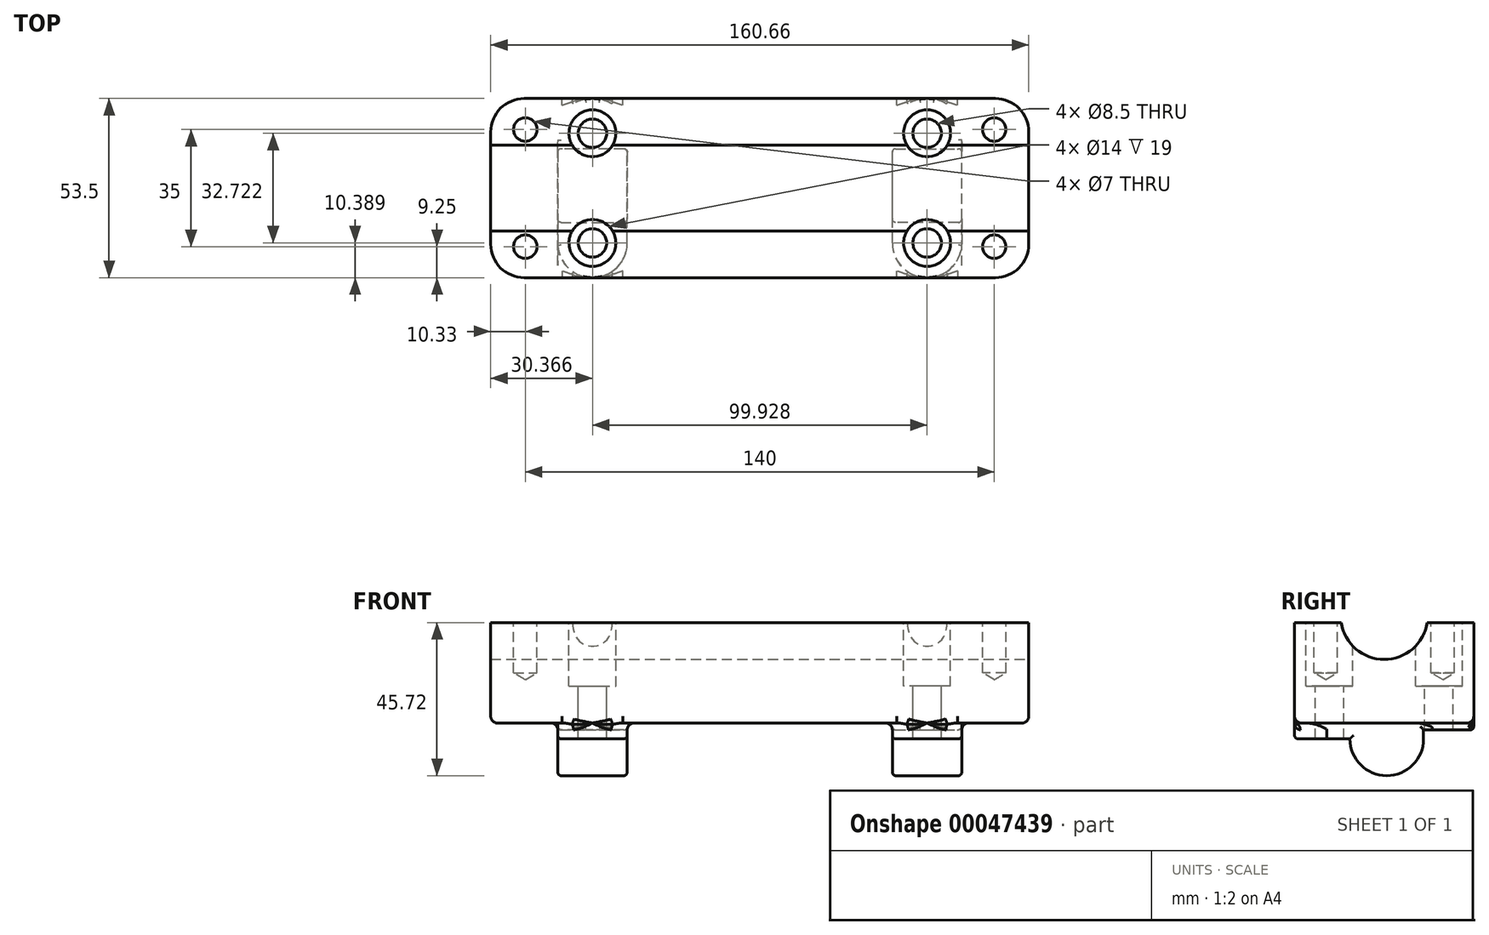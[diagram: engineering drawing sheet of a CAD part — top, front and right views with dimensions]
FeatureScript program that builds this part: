
annotation { "Feature Type Name" : "Feature", "Feature Type Description" : "" }
export const myFeature = defineFeature(function(context is Context, id is Id, definition is map)
    precondition{}
    {
        {
            var Q0;
            Q0=qCreatedBy(makeId("Right.planeOp"),FACE);
            var sketch = newSketch(context, id + "F0", { "sketchPlane" : qUnion([Q0])});
            skLineSegment(sketch, "E0.rect.bottom", {"start": v(-26.75, 15) * mm, "end": v(26.75, 15) * mm});
            skLineSegment(sketch, "E0.rect.top", {"start": v(-26.75, -15) * mm, "end": v(26.75, -15) * mm});
            skLineSegment(sketch, "E0.rect.left", {"start": v(-26.75, 15) * mm, "end": v(-26.75, -15) * mm});
            skLineSegment(sketch, "E0.rect.right", {"start": v(26.75, 15) * mm, "end": v(26.75, -15) * mm});
            skPoint(sketch, "E0.rect.middle", {"position": v(0, 0) * mm});
            skArc(sketch, "E1", {"start": v(-11, -15) * mm, "mid": v(0, -26) * mm, "end": v(11, -15) * mm, "construction": true});
            skLineSegment(sketch, "E2", {"start": v(0, 54.91) * mm, "end": v(0, -57.89) * mm, "construction": true});
            skLineSegment(sketch, "E3", {"start": v(45.54, 0) * mm, "end": v(-46.43, 0) * mm, "construction": true});
            skSolve(sketch);
        }
        {
            var Q0;
            Q0 = qSketchRegion(id + "F0", true);
            extrude(context, id + "F1", {"entities" : qUnion([Q0]), "depth" : 60.33 * mm});
        }
        {
            var Q0;
            Q0=makeQuery(id+"F1.opExtrude","SWEPT_FACE",FACE,{"disambiguationData":[OSD([sQuery(id+"F0.wireOp",EDGE,"E0.rect.top")])]});
            var sketch = newSketch(context, id + "F2", { "sketchPlane" : qUnion([Q0])});
            skLineSegment(sketch, "E4.left", {"start": v(60.33, 17.12) * mm, "end": v(60.33, -15.6) * mm});
            skLineSegment(sketch, "E4.right", {"start": v(39.58, 16.36) * mm, "end": v(39.58, -16.36) * mm});
            skArc(sketch, "E5", {"start": v(60.33, 17.12) * mm, "mid": v(49.58, 26.74) * mm, "end": v(39.58, 16.36) * mm});
            skArc(sketch, "E6", {"start": v(39.58, -16.36) * mm, "mid": v(50.35, -26.74) * mm, "end": v(60.33, -15.6) * mm});
            skSolve(sketch);
        }
        {
            var Q0;
            Q0 = qSketchRegion(id + "F2", true);
            extrude(context, id + "F3", {"entities" : qUnion([Q0]), "operationType" : NewBodyOperationType.ADD, "depth" : 2 * mm});
        }
        {
            var Q0;
            Q0=makeQuery(id+"F3.opExtrude","CAP_FACE",FACE,{"disambiguationData":[OSD([sQuery(id+"F2.wireOp",EDGE,"E4.bottom"),sQuery(id+"F2.wireOp",EDGE,"E4.top"),sQuery(id+"F2.wireOp",EDGE,"E4.left"),sQuery(id+"F2.wireOp",EDGE,"E4.right"),sQuery(id+"F2.wireOp",EDGE,"f8a1c87c-81db-4225-97d7-fa6d93f3a77e.filletArc"),sQuery(id+"F2.wireOp",EDGE,"b2d7f9ab-133a-4388-a99c-6f4bdffc8fad.filletArc"),sQuery(id+"F2.wireOp",EDGE,"5107bc96-7721-46f1-8cb8-a7f1d34a2143.filletArc"),sQuery(id+"F2.wireOp",EDGE,"96c77d12-6020-4846-88aa-47b855e8fed1.filletArc")])],"isStart":false});
            var sketch = newSketch(context, id + "F4", { "sketchPlane" : qUnion([Q0])});
            skLineSegment(sketch, "E7", {"start": v(60.33, 10.25) * mm, "end": v(39.58, 10.25) * mm});
            skLineSegment(sketch, "E8.0", {"start": v(39.58, 16.36) * mm, "end": v(39.58, 10.25) * mm});
            skArc(sketch, "E9.0", {"start": v(60.33, 17.12) * mm, "mid": v(49.58, 26.74) * mm, "end": v(39.58, 16.36) * mm});
            skLineSegment(sketch, "E10.0", {"start": v(60.33, 17.12) * mm, "end": v(60.33, 10.25) * mm});
            skPoint(sketch, "E11.orphan", {"position": v(39.58, -16.36) * mm});
            skPoint(sketch, "E12.orphan", {"position": v(60.33, -15.6) * mm});
            skSolve(sketch);
        }
        {
            var Q0;
            Q0 = qSketchRegion(id + "F4", true);
            extrude(context, id + "F5", {"entities" : qUnion([Q0]), "operationType" : NewBodyOperationType.ADD, "depth" : 2.72 * mm});
        }
        {
            var Q0;
            Q0=makeQuery(id+"F5.boolean.opBoolean","MERGE",FACE,{"derivedFrom":[makeQuery(id+"F3.boolean.opBoolean","MERGE",FACE,{"derivedFrom":[makeQuery(id+"F1.opExtrude","CAP_FACE",FACE,{"disambiguationData":[OSD([sQuery(id+"F0.wireOp",EDGE,"E0.rect.bottom"),sQuery(id+"F0.wireOp",EDGE,"E0.rect.top"),sQuery(id+"F0.wireOp",EDGE,"E0.rect.left"),sQuery(id+"F0.wireOp",EDGE,"E0.rect.right")])],"isStart":false}),makeQuery(id+"F3.opExtrude","SWEPT_FACE",FACE,{"disambiguationData":[OSD([sQuery(id+"F2.wireOp",EDGE,"E4.left")])]})]}),makeQuery(id+"F5.opExtrude","SWEPT_FACE",FACE,{"disambiguationData":[OSD([sQuery(id+"F4.wireOp",EDGE,"E10.0")])]})]});
            var sketch = newSketch(context, id + "F6", { "sketchPlane" : qUnion([Q0])});
            skArc(sketch, "E13", {"start": v(-10.25, -19.72) * mm, "mid": v(0.75, -30.72) * mm, "end": v(11.75, -19.72) * mm});
            skLineSegment(sketch, "E14", {"start": v(11.75, -19.72) * mm, "end": v(11.75, -17) * mm});
            skLineSegment(sketch, "E15", {"start": v(11.75, -17) * mm, "end": v(-10.25, -17) * mm});
            skLineSegment(sketch, "E16", {"start": v(-10.25, -17) * mm, "end": v(-10.25, -19.72) * mm});
            skSolve(sketch);
        }
        {
            var Q0;
            Q0 = qSketchRegion(id + "F6", true);
            var Q1;
            Q1=makeQuery(id+"F5.boolean.opBoolean","MERGE",FACE,{"derivedFrom":[makeQuery(id+"F3.opExtrude","SWEPT_FACE",FACE,{"disambiguationData":[OSD([sQuery(id+"F2.wireOp",EDGE,"E4.right")])]}),makeQuery(id+"F5.opExtrude","SWEPT_FACE",FACE,{"disambiguationData":[OSD([sQuery(id+"F4.wireOp",EDGE,"E8.0")])]})]});
            extrude(context, id + "F7", {"entities" : qUnion([Q0]), "operationType" : NewBodyOperationType.ADD, "endBound" : BoundingType.UP_TO_SURFACE, "oppositeDirection" : true, "endBoundEntityFace" : qUnion([Q1]), "depth" : 20 * mm});
        }
        {
            var Q0;
            Q0=makeQuery(id+"F1.opExtrude","CAP_FACE",FACE,{"disambiguationData":[OSD([sQuery(id+"F0.wireOp",EDGE,"E0.rect.bottom"),sQuery(id+"F0.wireOp",EDGE,"E0.rect.top"),sQuery(id+"F0.wireOp",EDGE,"E0.rect.left"),sQuery(id+"F0.wireOp",EDGE,"E0.rect.right")])],"isStart":false});
            var sketch = newSketch(context, id + "F8", { "sketchPlane" : qUnion([Q0])});
            skLineSegment(sketch, "E17.bottom", {"start": v(-26.75, 15) * mm, "end": v(26.75, 15) * mm});
            skLineSegment(sketch, "E17.top", {"start": v(-26.75, -15) * mm, "end": v(26.75, -15) * mm});
            skLineSegment(sketch, "E17.left", {"start": v(-26.75, 15) * mm, "end": v(-26.75, -15) * mm});
            skLineSegment(sketch, "E17.right", {"start": v(26.75, 15) * mm, "end": v(26.75, -15) * mm});
            skSolve(sketch);
        }
        {
            var Q0;
            Q0=makeQuery(id+"F8.imprint","IMPRINT",FACE,{"disambiguationData":[TD([[makeQuery(id+"F8.imprint","IMPRINT",EDGE,{"derivedFrom":makeQuery(id+"F1.opExtrude","CAP_EDGE",EDGE,{"disambiguationData":[OSD([sQuery(id+"F0.wireOp",EDGE,"E0.rect.bottom")])],"isStart":false})}),-1.0]])]});
            var Q1;
            Q1=makeQuery(id+"F8.imprint","IMPRINT",FACE,{"disambiguationData":[TD([[makeQuery(id+"F8.imprint","IMPRINT",EDGE,{"derivedFrom":sQuery(id+"F8.wireOp",EDGE,"E17.bottom")}),-1.0]])]});
            extrude(context, id + "F9", {"entities" : qUnion([Q0, Q1]), "operationType" : NewBodyOperationType.ADD, "depth" : 20 * mm});
        }
        {
            var Q0;
            Q0=makeQuery(id+"F9.boolean.opBoolean","MERGE",FACE,{"derivedFrom":[makeQuery(id+"F1.opExtrude","SWEPT_FACE",FACE,{"disambiguationData":[OSD([sQuery(id+"F0.wireOp",EDGE,"E0.rect.bottom")])]}),makeQuery(id+"F9.opExtrude","SWEPT_FACE",FACE,{"disambiguationData":[OSD([sQuery(id+"F8.wireOp",EDGE,"E17.bottom")])]})]});
            var sketch = newSketch(context, id + "F10", { "sketchPlane" : qUnion([Q0])});
            skLineSegment(sketch, "E18.0.0", {"start": v(39.58, -10.25) * mm, "end": v(60.33, -10.25) * mm});
            skLineSegment(sketch, "E18.0.1", {"start": v(60.33, -10.25) * mm, "end": v(60.33, -17.12) * mm});
            skArc(sketch, "E18.0.2", {"start": v(60.33, -17.12) * mm, "mid": v(49.58, -26.74) * mm, "end": v(39.58, -16.36) * mm});
            skLineSegment(sketch, "E18.0.3", {"start": v(39.58, -16.36) * mm, "end": v(39.58, -10.25) * mm});
            skLineSegment(sketch, "E19.0.0", {"start": v(60.32, 11.75) * mm, "end": v(39.58, 11.75) * mm});
            skLineSegment(sketch, "E19.0.1", {"start": v(39.58, 11.75) * mm, "end": v(39.58, 16.36) * mm});
            skArc(sketch, "E19.0.2", {"start": v(39.58, 16.36) * mm, "mid": v(50.35, 26.74) * mm, "end": v(60.33, 15.6) * mm});
            skLineSegment(sketch, "E19.0.3", {"start": v(60.33, 15.6) * mm, "end": v(60.33, 11.75) * mm});
            skSolve(sketch);
        }
        {
            var Q0;
            Q0=sQuery(id+"F10.wireOp",VERTEX,"E18.0.2.center");
            var Q1;
            Q1=sQuery(id+"F10.wireOp",VERTEX,"E19.0.2.center");
            var Q2;
            Q2=makeQuery(id+"F1.opExtrude","SWEPT_BODY",BODY,{"disambiguationData":[OSD([sQuery(id+"F0.wireOp",EDGE,"E0.rect.bottom"),sQuery(id+"F0.wireOp",EDGE,"E0.rect.top"),sQuery(id+"F0.wireOp",EDGE,"E0.rect.left"),sQuery(id+"F0.wireOp",EDGE,"E0.rect.right")])]});
            hole(context, id + "F11", {"style" : HoleStyle.C_BORE, "holeDiameter" : 8.5 * mm, "cBoreDiameter" : 14 * mm, "cBoreDepth" : 19 * mm, "endStyle" : HoleEndStyle.THROUGH, "locations" : qUnion([Q0, Q1]), "scope" : qUnion([Q2])});
        }
        {
            var Q0;
            Q0=makeQuery(id+"F9.boolean.opBoolean","MERGE",FACE,{"derivedFrom":[makeQuery(id+"F1.opExtrude","SWEPT_FACE",FACE,{"disambiguationData":[OSD([sQuery(id+"F0.wireOp",EDGE,"E0.rect.bottom")])]}),makeQuery(id+"F9.opExtrude","SWEPT_FACE",FACE,{"disambiguationData":[OSD([sQuery(id+"F8.wireOp",EDGE,"E17.bottom")])]})]});
            var sketch = newSketch(context, id + "F12", { "sketchPlane" : qUnion([Q0])});
            skPoint(sketch, "E20", {"position": v(70, 17.5) * mm});
            skPoint(sketch, "E21", {"position": v(70, -17.5) * mm});
            skLineSegment(sketch, "E22", {"start": v(80.33, 0) * mm, "end": v(0, 0) * mm, "construction": true});
            skSolve(sketch);
        }
        {
            var Q0;
            Q0=sQuery(id+"F12.wireOp",VERTEX,"E21");
            var Q1;
            Q1=sQuery(id+"F12.wireOp",VERTEX,"E20");
            var Q2;
            Q2=makeQuery(id+"F1.opExtrude","SWEPT_BODY",BODY,{"disambiguationData":[OSD([sQuery(id+"F0.wireOp",EDGE,"E0.rect.bottom"),sQuery(id+"F0.wireOp",EDGE,"E0.rect.top"),sQuery(id+"F0.wireOp",EDGE,"E0.rect.left"),sQuery(id+"F0.wireOp",EDGE,"E0.rect.right")])]});
            hole(context, id + "F13", {"style" : HoleStyle.SIMPLE, "holeDiameter" : 7 * mm, "endStyle" : HoleEndStyle.BLIND, "holeDepth" : 15 * mm, "locations" : qUnion([Q0, Q1]), "scope" : qUnion([Q2])});
        }
        {
            var Q0;
            Q0=makeQuery(id+"F1.opExtrude","SWEPT_BODY",BODY,{"disambiguationData":[OSD([sQuery(id+"F0.wireOp",EDGE,"E0.rect.bottom"),sQuery(id+"F0.wireOp",EDGE,"E0.rect.top"),sQuery(id+"F0.wireOp",EDGE,"E0.rect.left"),sQuery(id+"F0.wireOp",EDGE,"E0.rect.right")])]});
            var Q1;
            Q1=qCreatedBy(makeId("Right.planeOp"),FACE);
            mirror(context, id + "F14", {"operationType" : NewBodyOperationType.ADD, "entities" : qUnion([Q0]), "mirrorPlane" : qUnion([Q1])});
        }
        {
            var Q0;
            Q0=makeQuery(id+"F9.opExtrude","CAP_FACE",FACE,{"disambiguationData":[OSD([sQuery(id+"F8.wireOp",EDGE,"E17.bottom"),sQuery(id+"F8.wireOp",EDGE,"E17.top"),sQuery(id+"F8.wireOp",EDGE,"E17.left"),sQuery(id+"F8.wireOp",EDGE,"E17.right")])],"isStart":false});
            var sketch = newSketch(context, id + "F15", { "sketchPlane" : qUnion([Q0])});
            skCircle(sketch, "E23", {"center": v(0, 17) * mm, "radius": 13 * mm});
            skLineSegment(sketch, "E24", {"start": v(0, 17) * mm, "end": v(0, 15) * mm, "construction": true});
            skSolve(sketch);
        }
        {
            var Q0;
            Q0 = qSketchRegion(id + "F15", true);
            extrude(context, id + "F16", {"entities" : qUnion([Q0]), "operationType" : NewBodyOperationType.REMOVE, "endBound" : BoundingType.THROUGH_ALL, "oppositeDirection" : true, "depth" : 25 * mm});
        }
        {
            var Q0;
            Q0=makeQuery(id+"F14.opPattern","COPY",EDGE,{"derivedFrom":makeQuery(id+"F9.opExtrude","CAP_EDGE",EDGE,{"disambiguationData":[OSD([sQuery(id+"F8.wireOp",EDGE,"E17.left")])],"isStart":false}),"instanceName":"1"});
            var Q1;
            Q1=makeQuery(id+"F14.opPattern","COPY",EDGE,{"derivedFrom":makeQuery(id+"F9.opExtrude","CAP_EDGE",EDGE,{"disambiguationData":[OSD([sQuery(id+"F8.wireOp",EDGE,"E17.right")])],"isStart":false}),"instanceName":"1"});
            var Q2;
            Q2=makeQuery(id+"F9.opExtrude","CAP_EDGE",EDGE,{"disambiguationData":[OSD([sQuery(id+"F8.wireOp",EDGE,"E17.left")])],"isStart":false});
            var Q3;
            Q3=makeQuery(id+"F9.opExtrude","CAP_EDGE",EDGE,{"disambiguationData":[OSD([sQuery(id+"F8.wireOp",EDGE,"E17.right")])],"isStart":false});
            fillet(context, id + "F17", {"entities" : qUnion([Q0, Q1, Q2, Q3]), "radius" : 10 * mm, "tangentPropagation" : true, "allowEdgeOverflow" : false});
        }
        {
            var Q0;
            {var subQ0=sQuery(id+"F2.wireOp",EDGE,"E6");Q0=makeQuery(id+"F14.opPattern","COPY",EDGE,{"derivedFrom":makeQuery(id+"F3.boolean.opBoolean","SPLIT",EDGE,{"disambiguationData":[TD([makeQuery(id+"F1.opExtrude","SWEPT_FACE",FACE,{"disambiguationData":[OSD([sQuery(id+"F0.wireOp",EDGE,"E0.rect.top")])]}),makeQuery(id+"F1.opExtrude","SWEPT_FACE",FACE,{"disambiguationData":[OSD([sQuery(id+"F0.wireOp",EDGE,"E0.rect.right")])]}),makeQuery(id+"F3.opExtrude","SWEPT_FACE",FACE,{"disambiguationData":[OSD([sQuery(id+"F2.wireOp",EDGE,"E4.right")])]}),makeQuery(id+"F3.opExtrude","SWEPT_FACE",FACE,{"disambiguationData":[OSD([subQ0])]})])],"derivedFrom":makeQuery(id+"F3.opExtrude","CAP_EDGE",EDGE,{"disambiguationData":[OSD([subQ0])],"isStart":true})}),"instanceName":"1"});}
            var Q1;
            {var subQ0=sQuery(id+"F2.wireOp",EDGE,"E6");var subQ1=makeQuery(id+"F3.opExtrude","CAP_EDGE",EDGE,{"disambiguationData":[OSD([subQ0])],"isStart":true});var subQ2=makeQuery(id+"F3.opExtrude","SWEPT_FACE",FACE,{"disambiguationData":[OSD([subQ0])]});var subQ3=sQuery(id+"F0.wireOp",EDGE,"E0.rect.top");var subQ4=sQuery(id+"F0.wireOp",EDGE,"E0.rect.right");var subQ5=makeQuery(id+"F1.opExtrude","CAP_FACE",FACE,{"disambiguationData":[OSD([sQuery(id+"F0.wireOp",EDGE,"E0.rect.bottom"),subQ3,sQuery(id+"F0.wireOp",EDGE,"E0.rect.left"),subQ4])],"isStart":false});var subQ6=makeQuery(id+"F1.opExtrude","SWEPT_FACE",FACE,{"disambiguationData":[OSD([subQ3])]});var subQ7=sQuery(id+"F2.wireOp",EDGE,"E4.left");var subQ8=makeQuery(id+"F3.opExtrude","SWEPT_FACE",FACE,{"disambiguationData":[OSD([subQ7])]});var subQ9=makeQuery(id+"F3.opExtrude","CAP_FACE",FACE,{"disambiguationData":[OSD([subQ7,sQuery(id+"F2.wireOp",EDGE,"E4.right"),sQuery(id+"F2.wireOp",EDGE,"E5"),subQ0])],"isStart":true});Q1=makeQuery(id+"F14.opPattern","COPY",EDGE,{"derivedFrom":makeQuery(id+"F9.boolean.opBoolean","MERGE",EDGE,{"derivedFrom":[makeQuery(id+"F3.boolean.opBoolean","SPLIT",EDGE,{"disambiguationData":[TD([subQ5,subQ6,subQ8,subQ9,subQ2])],"derivedFrom":subQ1}),makeQuery(id+"F3.boolean.opBoolean","SPLIT",EDGE,{"disambiguationData":[TD([subQ5,subQ6,makeQuery(id+"F1.opExtrude","SWEPT_FACE",FACE,{"disambiguationData":[OSD([subQ4])]}),subQ8,subQ9,subQ2])],"derivedFrom":subQ1})]}),"instanceName":"1"});}
            var Q2;
            Q2=makeQuery(id+"F14.opPattern","COPY",EDGE,{"derivedFrom":makeQuery(id+"F9.opExtrude","CAP_EDGE",EDGE,{"disambiguationData":[OSD([sQuery(id+"F8.wireOp",EDGE,"E17.top")])],"isStart":true}),"instanceName":"1"});
            var Q3;
            Q3=makeQuery(id+"F9.opExtrude","CAP_EDGE",EDGE,{"disambiguationData":[OSD([sQuery(id+"F8.wireOp",EDGE,"E17.top")])],"isStart":true});
            var Q4;
            Q4=makeQuery(id+"F3.opExtrude","CAP_EDGE",EDGE,{"disambiguationData":[OSD([sQuery(id+"F2.wireOp",EDGE,"E4.right")])],"isStart":true});
            fillet(context, id + "F18", {"entities" : qUnion([Q0, Q1, Q2, Q3, Q4]), "radius" : 2 * mm, "tangentPropagation" : true, "allowEdgeOverflow" : false});
        }
        {
            var Q0;
            {var subQ0=sQuery(id+"F0.wireOp",EDGE,"E0.rect.top");var subQ1=sQuery(id+"F0.wireOp",EDGE,"E0.rect.left");var subQ2=makeQuery(id+"F3.boolean.opBoolean","SPLIT",EDGE,{"disambiguationData":[TD([makeQuery(id+"F1.opExtrude","CAP_FACE",FACE,{"disambiguationData":[OSD([sQuery(id+"F0.wireOp",EDGE,"E0.rect.bottom"),subQ0,subQ1,sQuery(id+"F0.wireOp",EDGE,"E0.rect.right")])],"isStart":true})])],"derivedFrom":makeQuery(id+"F1.opExtrude","SWEPT_EDGE",EDGE,{"disambiguationData":[OSD([subQ0,subQ1])]})});Q0=makeQuery(id+"F14.boolean.opBoolean","MERGE",EDGE,{"derivedFrom":[subQ2,makeQuery(id+"F14.opPattern","COPY",EDGE,{"derivedFrom":subQ2,"instanceName":"1"})]});}
            var Q1;
            {var subQ0=sQuery(id+"F0.wireOp",EDGE,"E0.rect.top");var subQ1=sQuery(id+"F0.wireOp",EDGE,"E0.rect.left");Q1=makeQuery(id+"F14.opPattern","COPY",EDGE,{"derivedFrom":makeQuery(id+"F9.boolean.opBoolean","MERGE",EDGE,{"derivedFrom":[makeQuery(id+"F3.boolean.opBoolean","SPLIT",EDGE,{"disambiguationData":[TD([makeQuery(id+"F3.opExtrude","SWEPT_FACE",FACE,{"disambiguationData":[OSD([sQuery(id+"F2.wireOp",EDGE,"E4.left")])]})])],"derivedFrom":makeQuery(id+"F1.opExtrude","SWEPT_EDGE",EDGE,{"disambiguationData":[OSD([subQ0,subQ1])]})}),makeQuery(id+"F9.opExtrude","SWEPT_EDGE",EDGE,{"disambiguationData":[OSD([sQuery(id+"F8.wireOp",EDGE,"E17.top"),sQuery(id+"F8.wireOp",EDGE,"E17.left")])]})]}),"instanceName":"1"});}
            var Q2;
            {var subQ0=sQuery(id+"F0.wireOp",EDGE,"E0.rect.top");var subQ1=sQuery(id+"F0.wireOp",EDGE,"E0.rect.right");var subQ2=makeQuery(id+"F3.boolean.opBoolean","SPLIT",EDGE,{"disambiguationData":[TD([makeQuery(id+"F1.opExtrude","CAP_FACE",FACE,{"disambiguationData":[OSD([sQuery(id+"F0.wireOp",EDGE,"E0.rect.bottom"),subQ0,sQuery(id+"F0.wireOp",EDGE,"E0.rect.left"),subQ1])],"isStart":true})])],"derivedFrom":makeQuery(id+"F1.opExtrude","SWEPT_EDGE",EDGE,{"disambiguationData":[OSD([subQ0,subQ1])]})});Q2=makeQuery(id+"F14.boolean.opBoolean","MERGE",EDGE,{"derivedFrom":[subQ2,makeQuery(id+"F14.opPattern","COPY",EDGE,{"derivedFrom":subQ2,"instanceName":"1"})]});}
            var Q3;
            {var subQ0=sQuery(id+"F0.wireOp",EDGE,"E0.rect.top");var subQ1=sQuery(id+"F0.wireOp",EDGE,"E0.rect.right");Q3=makeQuery(id+"F9.boolean.opBoolean","MERGE",EDGE,{"derivedFrom":[makeQuery(id+"F3.boolean.opBoolean","SPLIT",EDGE,{"disambiguationData":[TD([makeQuery(id+"F3.opExtrude","SWEPT_FACE",FACE,{"disambiguationData":[OSD([sQuery(id+"F2.wireOp",EDGE,"E4.left")])]})])],"derivedFrom":makeQuery(id+"F1.opExtrude","SWEPT_EDGE",EDGE,{"disambiguationData":[OSD([subQ0,subQ1])]})}),makeQuery(id+"F9.opExtrude","SWEPT_EDGE",EDGE,{"disambiguationData":[OSD([sQuery(id+"F8.wireOp",EDGE,"E17.top"),sQuery(id+"F8.wireOp",EDGE,"E17.right")])]})]});}
            fillet(context, id + "F19", {"entities" : qUnion([Q0, Q1, Q2, Q3]), "radius" : 2 * mm, "tangentPropagation" : true, "allowEdgeOverflow" : false});
        }
        {
            var Q0;
            Q0=makeQuery(id+"F14.opPattern","COPY",EDGE,{"derivedFrom":makeQuery(id+"F5.opExtrude","CAP_EDGE",EDGE,{"disambiguationData":[OSD([sQuery(id+"F4.wireOp",EDGE,"E9.0")])],"isStart":false}),"instanceName":"1"});
            var Q1;
            Q1=makeQuery(id+"F14.opPattern","COPY",EDGE,{"derivedFrom":makeQuery(id+"F7.opExtrude","CAP_EDGE",EDGE,{"disambiguationData":[OSD([sQuery(id+"F6.wireOp",EDGE,"E13")])],"isStart":true}),"instanceName":"1"});
            var Q2;
            Q2=makeQuery(id+"F14.opPattern","COPY",EDGE,{"derivedFrom":makeQuery(id+"F7.opExtrude","CAP_EDGE",EDGE,{"disambiguationData":[OSD([sQuery(id+"F6.wireOp",EDGE,"E13")])],"isStart":false}),"instanceName":"1"});
            var Q3;
            {var subQ0=sQuery(id+"F2.wireOp",EDGE,"E6");var subQ1=makeQuery(id+"F3.opExtrude","CAP_EDGE",EDGE,{"disambiguationData":[OSD([subQ0])],"isStart":true});var subQ2=makeQuery(id+"F3.opExtrude","SWEPT_FACE",FACE,{"disambiguationData":[OSD([subQ0])]});var subQ3=sQuery(id+"F0.wireOp",EDGE,"E0.rect.top");var subQ4=sQuery(id+"F0.wireOp",EDGE,"E0.rect.right");var subQ5=makeQuery(id+"F1.opExtrude","CAP_FACE",FACE,{"disambiguationData":[OSD([sQuery(id+"F0.wireOp",EDGE,"E0.rect.bottom"),subQ3,sQuery(id+"F0.wireOp",EDGE,"E0.rect.left"),subQ4])],"isStart":false});var subQ6=makeQuery(id+"F1.opExtrude","SWEPT_FACE",FACE,{"disambiguationData":[OSD([subQ3])]});var subQ7=sQuery(id+"F2.wireOp",EDGE,"E4.left");var subQ8=makeQuery(id+"F3.opExtrude","SWEPT_FACE",FACE,{"disambiguationData":[OSD([subQ7])]});var subQ9=sQuery(id+"F2.wireOp",EDGE,"E4.right");var subQ10=sQuery(id+"F2.wireOp",EDGE,"E5");var subQ11=makeQuery(id+"F3.opExtrude","CAP_FACE",FACE,{"disambiguationData":[OSD([subQ7,subQ9,subQ10,subQ0])],"isStart":true});Q3=makeQuery(id+"F18.opFillet","BLEND_EDGE",EDGE,{"blendedFrom":[makeQuery(id+"F14.opPattern","COPY",EDGE,{"derivedFrom":makeQuery(id+"F9.boolean.opBoolean","MERGE",EDGE,{"derivedFrom":[makeQuery(id+"F3.boolean.opBoolean","SPLIT",EDGE,{"disambiguationData":[TD([subQ5,subQ6,subQ8,subQ11,subQ2])],"derivedFrom":subQ1}),makeQuery(id+"F3.boolean.opBoolean","SPLIT",EDGE,{"disambiguationData":[TD([subQ5,subQ6,makeQuery(id+"F1.opExtrude","SWEPT_FACE",FACE,{"disambiguationData":[OSD([subQ4])]}),subQ8,subQ11,subQ2])],"derivedFrom":subQ1})]}),"instanceName":"1"}),makeQuery(id+"F14.opPattern","COPY",FACE,{"derivedFrom":makeQuery(id+"F3.opExtrude","CAP_FACE",FACE,{"disambiguationData":[OSD([subQ7,subQ9,subQ10,subQ0])],"isStart":false}),"instanceName":"1"})],"blendedInto":[makeQuery(id+"F14.opPattern","COPY",FACE,{"derivedFrom":makeQuery(id+"F3.opExtrude","CAP_FACE",FACE,{"disambiguationData":[OSD([subQ7,subQ9,subQ10,subQ0])],"isStart":false}),"instanceName":"1"})]});}
            var Q4;
            Q4=makeQuery(id+"F7.opExtrude","CAP_EDGE",EDGE,{"disambiguationData":[OSD([sQuery(id+"F6.wireOp",EDGE,"E13")])],"isStart":true});
            var Q5;
            {var subQ0=sQuery(id+"F2.wireOp",EDGE,"E6");var subQ1=makeQuery(id+"F3.opExtrude","CAP_EDGE",EDGE,{"disambiguationData":[OSD([subQ0])],"isStart":true});var subQ2=makeQuery(id+"F3.opExtrude","SWEPT_FACE",FACE,{"disambiguationData":[OSD([subQ0])]});var subQ3=sQuery(id+"F0.wireOp",EDGE,"E0.rect.top");var subQ4=sQuery(id+"F0.wireOp",EDGE,"E0.rect.right");var subQ5=makeQuery(id+"F1.opExtrude","CAP_FACE",FACE,{"disambiguationData":[OSD([sQuery(id+"F0.wireOp",EDGE,"E0.rect.bottom"),subQ3,sQuery(id+"F0.wireOp",EDGE,"E0.rect.left"),subQ4])],"isStart":false});var subQ6=makeQuery(id+"F1.opExtrude","SWEPT_FACE",FACE,{"disambiguationData":[OSD([subQ3])]});var subQ7=sQuery(id+"F2.wireOp",EDGE,"E4.left");var subQ8=makeQuery(id+"F3.opExtrude","SWEPT_FACE",FACE,{"disambiguationData":[OSD([subQ7])]});var subQ9=sQuery(id+"F2.wireOp",EDGE,"E4.right");var subQ10=sQuery(id+"F2.wireOp",EDGE,"E5");var subQ11=makeQuery(id+"F3.opExtrude","CAP_FACE",FACE,{"disambiguationData":[OSD([subQ7,subQ9,subQ10,subQ0])],"isStart":true});Q5=makeQuery(id+"F18.opFillet","BLEND_EDGE",EDGE,{"blendedFrom":[makeQuery(id+"F9.boolean.opBoolean","MERGE",EDGE,{"derivedFrom":[makeQuery(id+"F3.boolean.opBoolean","SPLIT",EDGE,{"disambiguationData":[TD([subQ5,subQ6,subQ8,subQ11,subQ2])],"derivedFrom":subQ1}),makeQuery(id+"F3.boolean.opBoolean","SPLIT",EDGE,{"disambiguationData":[TD([subQ5,subQ6,makeQuery(id+"F1.opExtrude","SWEPT_FACE",FACE,{"disambiguationData":[OSD([subQ4])]}),subQ8,subQ11,subQ2])],"derivedFrom":subQ1})]}),makeQuery(id+"F3.opExtrude","CAP_FACE",FACE,{"disambiguationData":[OSD([subQ7,subQ9,subQ10,subQ0])],"isStart":false})],"blendedInto":[makeQuery(id+"F3.opExtrude","CAP_FACE",FACE,{"disambiguationData":[OSD([subQ7,subQ9,subQ10,subQ0])],"isStart":false})]});}
            var Q6;
            Q6=makeQuery(id+"F5.opExtrude","CAP_EDGE",EDGE,{"disambiguationData":[OSD([sQuery(id+"F4.wireOp",EDGE,"E9.0")])],"isStart":false});
            var Q7;
            Q7=makeQuery(id+"F7.opExtrude","CAP_EDGE",EDGE,{"disambiguationData":[OSD([sQuery(id+"F6.wireOp",EDGE,"E13")])],"isStart":false});
            fillet(context, id + "F20", {"entities" : qUnion([Q0, Q1, Q2, Q3, Q4, Q5, Q6, Q7]), "radius" : 1 * mm, "tangentPropagation" : true, "allowEdgeOverflow" : false});
        }
    });
